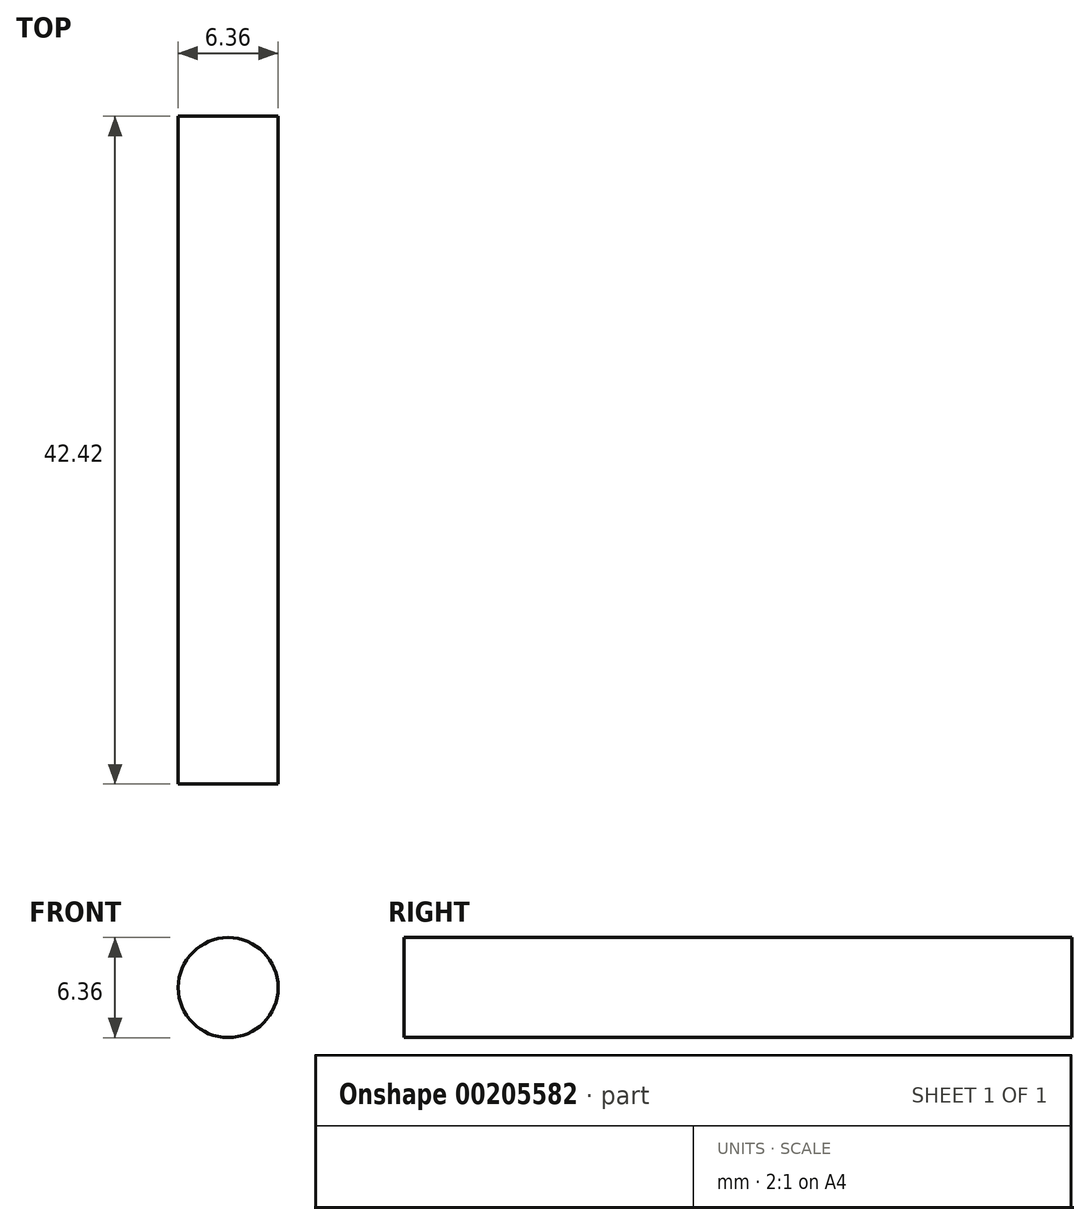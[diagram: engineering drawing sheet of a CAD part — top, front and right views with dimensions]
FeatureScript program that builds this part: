
annotation { "Feature Type Name" : "Feature", "Feature Type Description" : "" }
export const myFeature = defineFeature(function(context is Context, id is Id, definition is map)
    precondition{}
    {
        {
            var Q0;
            Q0=qCreatedBy(makeId("Front.planeOp"),FACE);
            var sketch = newSketch(context, id + "F0", { "sketchPlane" : qUnion([Q0])});
            skCircle(sketch, "E0", {"center": v(0, 0) * mm, "radius": 3.18 * mm});
            skSolve(sketch);
        }
        {
            var Q0;
            Q0=qSketchRegion(id+"F0",true);
            extrude(context, id + "F1", {"entities" : qUnion([Q0]), "depth" : 42.42 * mm});
        }
    });
